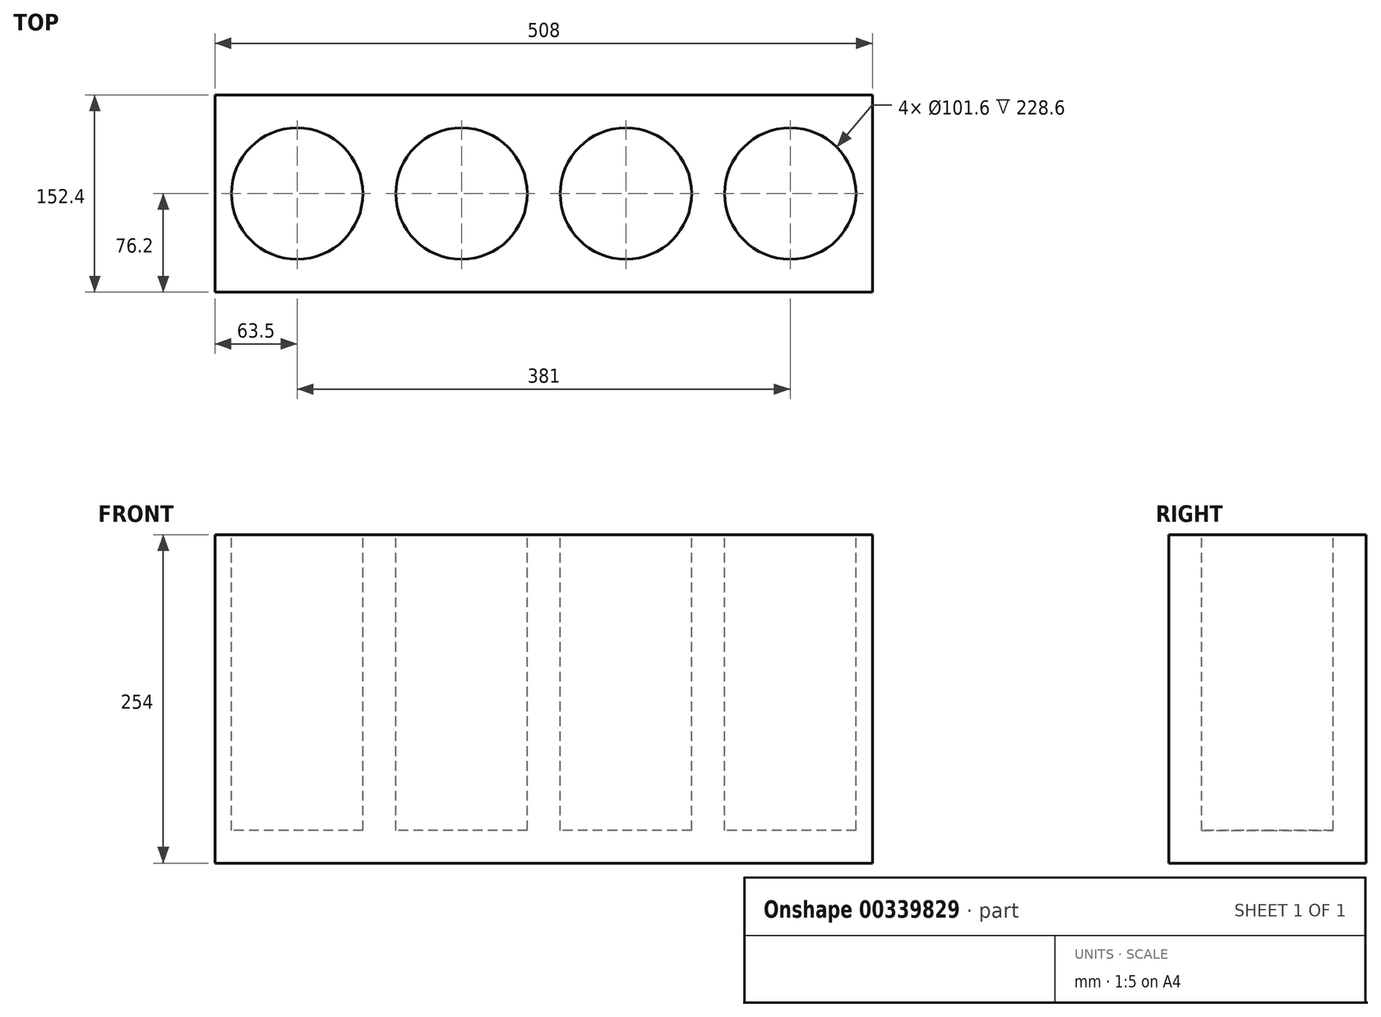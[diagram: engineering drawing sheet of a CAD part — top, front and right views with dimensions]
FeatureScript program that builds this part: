
annotation { "Feature Type Name" : "Feature", "Feature Type Description" : "" }
export const myFeature = defineFeature(function(context is Context, id is Id, definition is map)
    precondition{}
    {
        {
            var Q0;
            Q0=qCreatedBy(makeId("Top.planeOp"),FACE);
            var sketch = newSketch(context, id + "F0", { "sketchPlane" : qUnion([Q0])});
            skLineSegment(sketch, "E0.bottom", {"start": v(-254, 76.2) * mm, "end": v(254, 76.2) * mm});
            skLineSegment(sketch, "E0.top", {"start": v(-254, -76.2) * mm, "end": v(254, -76.2) * mm});
            skLineSegment(sketch, "E0.left", {"start": v(-254, 76.2) * mm, "end": v(-254, -76.2) * mm});
            skLineSegment(sketch, "E0.right", {"start": v(254, 76.2) * mm, "end": v(254, -76.2) * mm});
            skSolve(sketch);
        }
        {
            var Q0;
            Q0 = qSketchRegion(id + "F0", true);
            extrude(context, id + "F1", {"entities" : qUnion([Q0]), "oppositeDirection" : true, "depth" : 254 * mm});
        }
        {
            var Q0;
            Q0=makeQuery(id+"F1.opExtrude","CAP_FACE",FACE,{"disambiguationData":[OSD([sQuery(id+"F0.wireOp",EDGE,"E0.bottom"),sQuery(id+"F0.wireOp",EDGE,"E0.top"),sQuery(id+"F0.wireOp",EDGE,"E0.left"),sQuery(id+"F0.wireOp",EDGE,"E0.right")])],"isStart":true});
            var sketch = newSketch(context, id + "F2", { "sketchPlane" : qUnion([Q0])});
            skCircle(sketch, "E1", {"center": v(-63.5, 0) * mm, "radius": 50.8 * mm});
            skCircle(sketch, "E2", {"center": v(63.5, 0) * mm, "radius": 50.8 * mm});
            skCircle(sketch, "E3", {"center": v(-190.5, 0) * mm, "radius": 50.8 * mm});
            skCircle(sketch, "E4", {"center": v(190.5, 0) * mm, "radius": 50.8 * mm});
            skSolve(sketch);
        }
        {
            var Q0;
            Q0 = qSketchRegion(id + "F2", true);
            extrude(context, id + "F3", {"entities" : qUnion([Q0]), "operationType" : NewBodyOperationType.REMOVE, "oppositeDirection" : true, "depth" : 228.6 * mm});
        }
    });
